# Revit family: Hager-VECTOR-Surface_mounted-IP65-With_Cover-With_DIN-NoHosted-FR-fr
name_source: partatom
category: Electrical Equipment
units: mm (PartAtom-declared; Revit-internal decimal feet)

## family parameters
Always vertical = Yes
Cut with Voids When Loaded = No
Maintain Annotation Orientation = No
Panel Configuration = Two Columns, Circuits Across
Part Type = Panelboard
Room Calculation Point = No
Round Connector Dimension = Use Diameter
Shared = No
Work Plane-Based = Yes

## types (19) — shared parameters
Code hager = ADD-EC000214_EU
Default Elevation = 1200 mm
EF000003 - mode de pose = saillie
EF000007 - couleur = gris
EF000024 - résistant aux UV = No
EF000116 - numéro RAL = 7035
EF000118 - avec cadre/support de montage = No
EF001062 - finition CEM = No
EF001134 - rail DIN = Yes
EF004462 - type de fermeture = autre
EF005474 - indice de protection (IP) = IP65
EF006306 - avec serrure = No
EF015777 - borne à conducteur neutre = No
ETIM class code = EC000214
ETIM class name = Small distribution board
HG000001-nombre de colonnes = 1
HG000002-avec porte = Yes
HG000003-Gamme = VECTOR
HG000005-Epaisseur = 2 mm  [stored 0.00656168 ft]
HG000006-Encastré = No
HG000009-Porte à double battant = No
HG000010-Portes asymétriques = No
HG000011-Rangées du bas vides = No
HG000012-Angle de pivotement de la porte = 90.00°
HG000013-Porte à gauche = No
HG000014-Porte à droite = Yes
HG000015-Visibilité de l'emprise de la porte = Yes
HG000016-Visibilité de la porte 3D = Yes
HG000017-Distance entre pôles = 18 mm  [stored 0.0590551 ft]
HG000060-RAL-number = 7035
HG000099-ID modèle Onfly = 507532
Manufacturer = Hager
Name BIM&CO = Electricity
Name hager = ADD_Enclosures_EC000214
Reference = Template-Enclosure_EU-EC000214
Uniformat = Low Tension Service & Dist.
Uniformat code = D501001
zero-valued in all types: EF000218 - profondeur d'encastrement, EF000332 - hauteur d'encastrement, EF000846 - largeur d'encastrement, EF001131 - profondeur intérieure, HG000007-Nombre de colonnes vides, HG000008-Nombre de rangées vides

## per-type parameters (varying)
| type | BC_METADATA | EF000008 - largeur | EF000040 - hauteur | EF000049 - profondeur | EF000266 - nombre de rangées | EF001088 - possibilité de montage en saillie | EF002950 - largeur en nombre de modules | EF006244 - couvercle/porte transparent(e) | EF009212 - finition du couvercle | EF015776 - borne de mise à la terre | EF015941 - porte pour transmission du signal | HG000004-Référence fabricant | HGEF000266-Nombre de rangées | HGEF0002950-largeur en nombre de modules |
| VECTOR-Surface_mounted_W111_H175_D93_3_Modular_Spacing-VE103E | {"ObjectGuid":"e70a9e09-0f15-4b4a-a7bb-f3f77c1a9dc2","ModelGuid":"331d0ccd-d2f6-4e46-b546-0a2dee03d905","VariantGuid":"3cbeddc3-77d1-4591-b966-ee755bac720d","Revision":"#6","VariantName":"VECTOR-Surface_mounted_W111_H175_D93_3_Modular_Spacing-VE103E"} | 111 mm | 175 mm  [stored 0.574147 ft] | 93 mm  [stored 0.305118 ft] | 1 | Yes | 3 | Yes | fermé | No | Yes | VE103E | 1 | 3 |
| VECTOR-Surface_mounted_W111_H175_D93_3_Modular_Spacing-VE103F | {"ObjectGuid":"e70a9e09-0f15-4b4a-a7bb-f3f77c1a9dc2","ModelGuid":"331d0ccd-d2f6-4e46-b546-0a2dee03d905","VariantGuid":"a8f88960-b45a-4394-acd2-167fb0afcfb3","Revision":"#6","VariantName":"VECTOR-Surface_mounted_W111_H175_D93_3_Modular_Spacing-VE103F"} | 111 mm | 175 mm  [stored 0.574147 ft] | 93 mm  [stored 0.305118 ft] | 1 | No | 3 | No | fermé | No | No | VE103F | 1 | 3 |
| VECTOR-Surface_mounted_W165_H190_D113_6_Modular_Spacing-VE106F | {"ObjectGuid":"e70a9e09-0f15-4b4a-a7bb-f3f77c1a9dc2","ModelGuid":"331d0ccd-d2f6-4e46-b546-0a2dee03d905","VariantGuid":"2c93ffe6-f540-4e5b-926d-e182cd81c1c1","Revision":"#6","VariantName":"VECTOR-Surface_mounted_W165_H190_D113_6_Modular_Spacing-VE106F"} | 165 mm | 190 mm  [stored 0.62336 ft] | 113 mm  [stored 0.370735 ft] | 1 | Yes | 6 | No | fermé | Yes | Yes | VE106F | 1 | 6 |
| VECTOR-Surface_mounted_W237_H210_D114_10_Modular_Spacing-VE110E | {"ObjectGuid":"e70a9e09-0f15-4b4a-a7bb-f3f77c1a9dc2","ModelGuid":"331d0ccd-d2f6-4e46-b546-0a2dee03d905","VariantGuid":"69345f80-b227-4df7-8da4-7abef1c6eaa4","Revision":"#6","VariantName":"VECTOR-Surface_mounted_W237_H210_D114_10_Modular_Spacing-VE110E"} | 237 mm  [stored 0.777559 ft] | 210 mm  [stored 0.688976 ft] | 114 mm  [stored 0.374016 ft] | 1 | Yes | 10 | Yes | fermé | No | Yes | VE110E | 1 | 10 |
| VECTOR-Surface_mounted_W237_H210_D114_10_Modular_Spacing-VE110F | {"ObjectGuid":"e70a9e09-0f15-4b4a-a7bb-f3f77c1a9dc2","ModelGuid":"331d0ccd-d2f6-4e46-b546-0a2dee03d905","VariantGuid":"6d8ca64f-5de5-4525-ba17-f89335538605","Revision":"#6","VariantName":"VECTOR-Surface_mounted_W237_H210_D114_10_Modular_Spacing-VE110F"} | 237 mm  [stored 0.777559 ft] | 210 mm  [stored 0.688976 ft] | 114 mm  [stored 0.374016 ft] | 1 | Yes | 10 | No | fermé | Yes | Yes | VE110F | 1 | 10 |
| VECTOR-Surface_mounted_W310_H302_D151_12_Modular_Spacing-VE112E | {"ObjectGuid":"e70a9e09-0f15-4b4a-a7bb-f3f77c1a9dc2","ModelGuid":"331d0ccd-d2f6-4e46-b546-0a2dee03d905","VariantGuid":"fa7f18e8-3e23-4239-bdca-7b78788d59f6","Revision":"#6","VariantName":"VECTOR-Surface_mounted_W310_H302_D151_12_Modular_Spacing-VE112E"} | 310 mm  [stored 1.01706 ft] | 302 mm  [stored 0.990814 ft] | 151 mm  [stored 0.495407 ft] | 1 | Yes | 12 | Yes | fermé | No | Yes | VE112E | 1 | 12 |
| VECTOR-Surface_mounted_W310_H302_D151_12_Modular_Spacing-VE112F | {"ObjectGuid":"e70a9e09-0f15-4b4a-a7bb-f3f77c1a9dc2","ModelGuid":"331d0ccd-d2f6-4e46-b546-0a2dee03d905","VariantGuid":"2a336b11-fb1e-43e2-b71f-7ce2997365ec","Revision":"#6","VariantName":"VECTOR-Surface_mounted_W310_H302_D151_12_Modular_Spacing-VE112F"} | 310 mm  [stored 1.01706 ft] | 302 mm  [stored 0.990814 ft] | 151 mm  [stored 0.495407 ft] | 1 | Yes | 12 | No | fermé | Yes | Yes | VE112F | 1 | 12 |
| VECTOR-Surface_mounted_W418_H302_D151_18_Modular_Spacing-VE118E | {"ObjectGuid":"e70a9e09-0f15-4b4a-a7bb-f3f77c1a9dc2","ModelGuid":"331d0ccd-d2f6-4e46-b546-0a2dee03d905","VariantGuid":"f7575e8c-d027-4af7-a21e-40c0c88cdb51","Revision":"#6","VariantName":"VECTOR-Surface_mounted_W418_H302_D151_18_Modular_Spacing-VE118E"} | 418 mm  [stored 1.37139 ft] | 302 mm  [stored 0.990814 ft] | 151 mm  [stored 0.495407 ft] | 1 | Yes | 18 | Yes | fermé | No | Yes | VE118E | 1 | 18 |
| VECTOR-Surface_mounted_W418_H302_D151_18_Modular_Spacing-VE118F | {"ObjectGuid":"e70a9e09-0f15-4b4a-a7bb-f3f77c1a9dc2","ModelGuid":"331d0ccd-d2f6-4e46-b546-0a2dee03d905","VariantGuid":"85ec31a4-f912-4c4f-96a5-89f4f76bc674","Revision":"#6","VariantName":"VECTOR-Surface_mounted_W418_H302_D151_18_Modular_Spacing-VE118F"} | 418 mm  [stored 1.37139 ft] | 302 mm  [stored 0.990814 ft] | 151 mm  [stored 0.495407 ft] | 1 | No | 18 | No | fermé | No | No | VE118F | 1 | 18 |
| VECTOR-Surface_mounted_W310_H427_D151_12_Modular_Spacing-VE212E | {"ObjectGuid":"e70a9e09-0f15-4b4a-a7bb-f3f77c1a9dc2","ModelGuid":"331d0ccd-d2f6-4e46-b546-0a2dee03d905","VariantGuid":"42a63334-0517-433b-981c-243b60e50ef7","Revision":"#6","VariantName":"VECTOR-Surface_mounted_W310_H427_D151_12_Modular_Spacing-VE212E"} | 310 mm  [stored 1.01706 ft] | 427 mm  [stored 1.40092 ft] | 151 mm  [stored 0.495407 ft] | 2 | Yes | 12 | Yes | fermé | No | Yes | VE212E | 2 | 12 |
| VECTOR-Surface_mounted_W310_H427_D151_12_Modular_Spacing-VE212F | {"ObjectGuid":"e70a9e09-0f15-4b4a-a7bb-f3f77c1a9dc2","ModelGuid":"331d0ccd-d2f6-4e46-b546-0a2dee03d905","VariantGuid":"c030dc11-0112-4447-b5d5-0733e42c9145","Revision":"#6","VariantName":"VECTOR-Surface_mounted_W310_H427_D151_12_Modular_Spacing-VE212F"} | 310 mm  [stored 1.01706 ft] | 427 mm  [stored 1.40092 ft] | 151 mm  [stored 0.495407 ft] | 2 | Yes | 12 | No | fermé | Yes | Yes | VE212F | 2 | 12 |
| VECTOR-Surface_mounted_W418_H452_D151_12_Modular_Spacing-VE218E | {"ObjectGuid":"e70a9e09-0f15-4b4a-a7bb-f3f77c1a9dc2","ModelGuid":"331d0ccd-d2f6-4e46-b546-0a2dee03d905","VariantGuid":"6eb27715-8cae-433d-80e1-d412b3d74896","Revision":"#6","VariantName":"VECTOR-Surface_mounted_W418_H452_D151_12_Modular_Spacing-VE218E"} | 418 mm  [stored 1.37139 ft] | 452 mm  [stored 1.48294 ft] | 151 mm  [stored 0.495407 ft] | 2 | Yes | 12 | Yes | avec échancrure | No | Yes | VE218E | 2 | 12 |
| VECTOR-Surface_mounted_W418_H452_D151_18_Modular_Spacing-VE218F | {"ObjectGuid":"e70a9e09-0f15-4b4a-a7bb-f3f77c1a9dc2","ModelGuid":"331d0ccd-d2f6-4e46-b546-0a2dee03d905","VariantGuid":"6b88fa11-b46a-4a4f-ad28-2851db47eeb2","Revision":"#6","VariantName":"VECTOR-Surface_mounted_W418_H452_D151_18_Modular_Spacing-VE218F"} | 418 mm  [stored 1.37139 ft] | 452 mm  [stored 1.48294 ft] | 151 mm  [stored 0.495407 ft] | 2 | No | 18 | No | avec échancrure | No | No | VE218F | 2 | 18 |
| VECTOR-Surface_mounted_W310_H552_D151_12_Modular_Spacing-VE312E | {"ObjectGuid":"e70a9e09-0f15-4b4a-a7bb-f3f77c1a9dc2","ModelGuid":"331d0ccd-d2f6-4e46-b546-0a2dee03d905","VariantGuid":"a51360fb-be86-40c0-8eea-6738b20dca28","Revision":"#6","VariantName":"VECTOR-Surface_mounted_W310_H552_D151_12_Modular_Spacing-VE312E"} | 310 mm  [stored 1.01706 ft] | 552 mm  [stored 1.81102 ft] | 151 mm  [stored 0.495407 ft] | 3 | Yes | 12 | Yes | fermé | No | Yes | VE312E | 3 | 12 |
| VECTOR-Surface_mounted_W310_H552_D151_12_Modular_Spacing-VE312F | {"ObjectGuid":"e70a9e09-0f15-4b4a-a7bb-f3f77c1a9dc2","ModelGuid":"331d0ccd-d2f6-4e46-b546-0a2dee03d905","VariantGuid":"db0fb16c-8394-4f9c-a336-45c0c0fab06d","Revision":"#6","VariantName":"VECTOR-Surface_mounted_W310_H552_D151_12_Modular_Spacing-VE312F"} | 310 mm  [stored 1.01706 ft] | 552 mm  [stored 1.81102 ft] | 151 mm  [stored 0.495407 ft] | 3 | Yes | 12 | No | fermé | Yes | Yes | VE312F | 3 | 12 |
| VECTOR-Surface_mounted_W418_H602_D151_12_Modular_Spacing-VE318E | {"ObjectGuid":"e70a9e09-0f15-4b4a-a7bb-f3f77c1a9dc2","ModelGuid":"331d0ccd-d2f6-4e46-b546-0a2dee03d905","VariantGuid":"618cf0b5-f35e-4738-9dd5-f075f16fe7af","Revision":"#6","VariantName":"VECTOR-Surface_mounted_W418_H602_D151_12_Modular_Spacing-VE318E"} | 418 mm  [stored 1.37139 ft] | 602 mm  [stored 1.97507 ft] | 151 mm  [stored 0.495407 ft] | 3 | Yes | 12 | Yes | avec échancrure | No | Yes | VE318E | 3 | 12 |
| VECTOR-Surface_mounted_W418_H602_D151_18_Modular_Spacing-VE318F | {"ObjectGuid":"e70a9e09-0f15-4b4a-a7bb-f3f77c1a9dc2","ModelGuid":"331d0ccd-d2f6-4e46-b546-0a2dee03d905","VariantGuid":"50c8a527-75ab-42ee-9dc0-89edf3a37759","Revision":"#6","VariantName":"VECTOR-Surface_mounted_W418_H602_D151_18_Modular_Spacing-VE318F"} | 418 mm  [stored 1.37139 ft] | 602 mm  [stored 1.97507 ft] | 151 mm  [stored 0.495407 ft] | 3 | No | 18 | No | avec échancrure | No | No | VE318F | 3 | 18 |
| VECTOR-Surface_mounted_W310_H677_D151_12_Modular_Spacing-VE412E | {"ObjectGuid":"e70a9e09-0f15-4b4a-a7bb-f3f77c1a9dc2","ModelGuid":"331d0ccd-d2f6-4e46-b546-0a2dee03d905","VariantGuid":"da480619-4630-4960-b63a-62301c31f6e6","Revision":"#6","VariantName":"VECTOR-Surface_mounted_W310_H677_D151_12_Modular_Spacing-VE412E"} | 310 mm  [stored 1.01706 ft] | 677 mm  [stored 2.22113 ft] | 151 mm  [stored 0.495407 ft] | 4 | No | 12 | No | avec échancrure | No | No | VE412E | 4 | 12 |
| VECTOR-Surface_mounted_W310_H677_D151_12_Modular_Spacing-VE412F | {"ObjectGuid":"e70a9e09-0f15-4b4a-a7bb-f3f77c1a9dc2","ModelGuid":"331d0ccd-d2f6-4e46-b546-0a2dee03d905","VariantGuid":"b246fd04-eff7-4812-afc8-41a9e78025f9","Revision":"#6","VariantName":"VECTOR-Surface_mounted_W310_H677_D151_12_Modular_Spacing-VE412F"} | 310 mm  [stored 1.01706 ft] | 677 mm  [stored 2.22113 ft] | 151 mm  [stored 0.495407 ft] | 4 | No | 12 | No | avec échancrure | No | No | VE412F | 4 | 12 |

note: [stored X ft] marks values corroborated as IEEE doubles in the binary element streams (Revit-internal decimal feet)

## geometry (parser evidence)
native form markers: Sweep x15
no freeform markers — native parametric forms only
